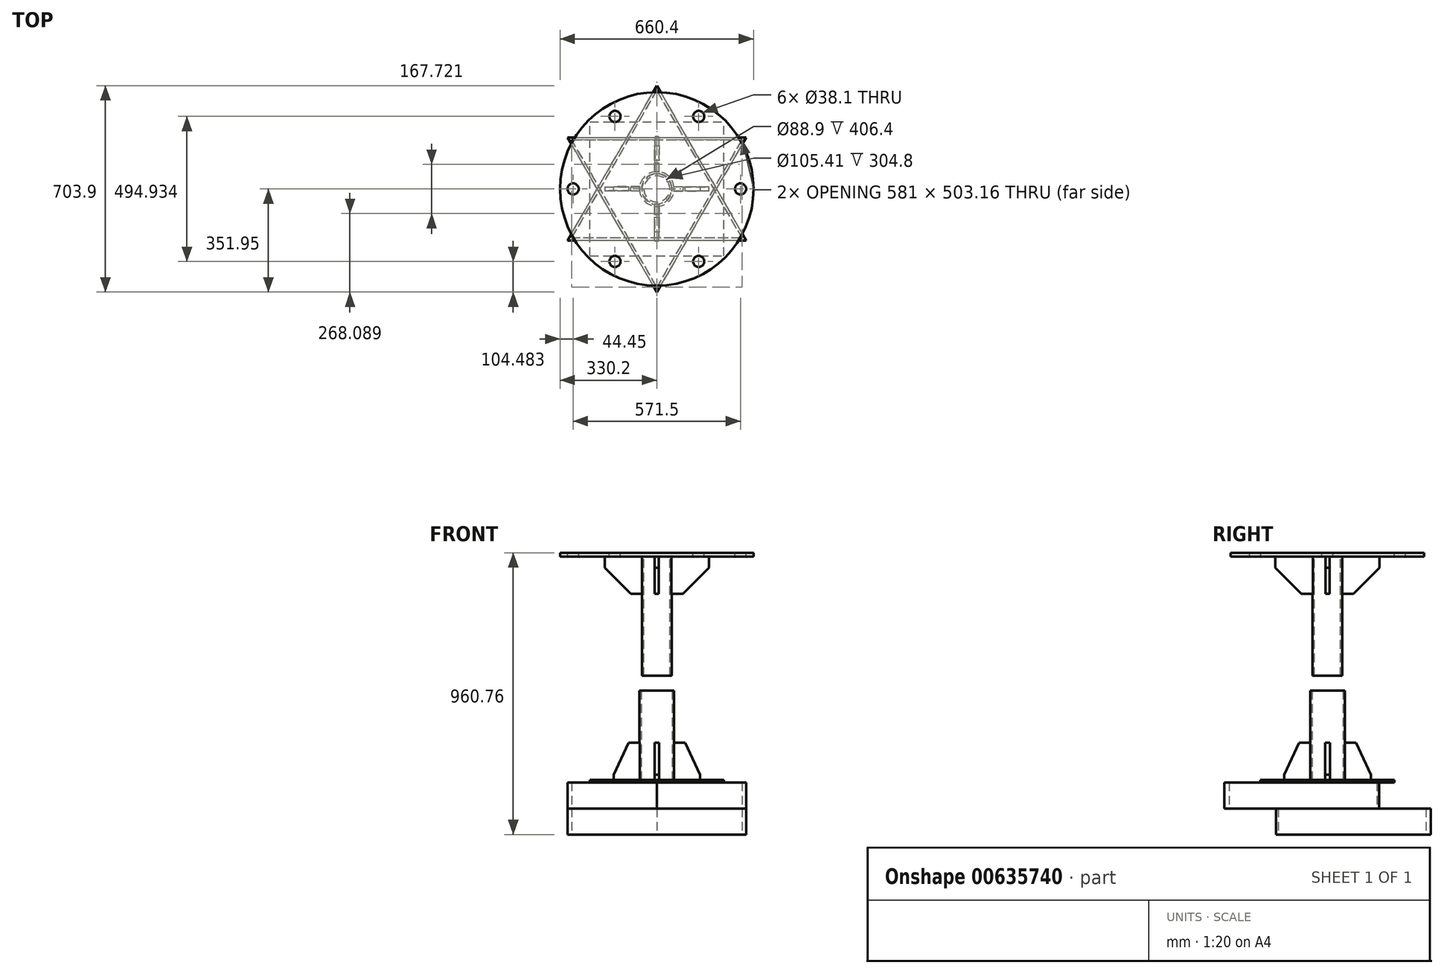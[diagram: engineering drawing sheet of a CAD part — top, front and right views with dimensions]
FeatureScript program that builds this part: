
annotation { "Feature Type Name" : "Feature", "Feature Type Description" : "" }
export const myFeature = defineFeature(function(context is Context, id is Id, definition is map)
    precondition{}
    {
        {
            var Q0;
            Q0=qCreatedBy(makeId("Top.planeOp"),FACE);
            var sketch = newSketch(context, id + "F0", { "sketchPlane" : qUnion([Q0])});
            skPoint(sketch, "E0.middle", {"position": v(0, 0) * mm});
            skCircle(sketch, "E1.cCircle", {"center": v(0, 0) * mm, "radius": 175.98 * mm, "construction": true});
            skLineSegment(sketch, "E1.0", {"start": v(304.8, -175.98) * mm, "end": v(-304.8, -175.98) * mm});
            skLineSegment(sketch, "E1.1", {"start": v(-304.8, -175.98) * mm, "end": v(0, 351.95) * mm});
            skLineSegment(sketch, "E1.2", {"start": v(0, 351.95) * mm, "end": v(304.8, -175.98) * mm});
            skPoint(sketch, "E1.0.midPoint", {"position": v(0, -175.98) * mm});
            skPoint(sketch, "E2.0.midPoint", {"position": v(-152.4, -87.99) * mm});
            skLineSegment(sketch, "E3.0", {"start": v(-290.5, -167.72) * mm, "end": v(0, 335.44) * mm});
            skLineSegment(sketch, "E3.1", {"start": v(290.5, -167.72) * mm, "end": v(-290.5, -167.72) * mm});
            skLineSegment(sketch, "E3.2", {"start": v(0, 335.44) * mm, "end": v(290.5, -167.72) * mm});
            skSolve(sketch);
        }
        {
            var Q0;
            Q0=qSketchRegion(id+"F0",true);
            var Q1;
            Q1=qConstructionFilter(qBodyType(qCreatedBy(id+"F0",EDGE),BodyType.WIRE),ConstructionObject.NO);
            extrude(context, id + "F1", {"entities" : qUnion([Q0]), "surfaceEntities" : qUnion([Q1]), "depth" : 88.9 * mm, "offsetDistance" : 25.4 * mm});
        }
        {
            var Q0;
            Q0=qCreatedBy(makeId("Top.planeOp"),FACE);
            cPlane(context, id + "F2", {"entities" : qUnion([Q0]), "cplaneType" : CPlaneType.OFFSET, "offset" : 88.9 * mm, "width" : 152.4 * mm, "height" : 152.4 * mm});
        }
        {
            var Q0;
            Q0=qCreatedBy(id+"F2.planeOp",FACE);
            var sketch = newSketch(context, id + "F3", { "sketchPlane" : qUnion([Q0])});
            skCircle(sketch, "E4.cCircle", {"center": v(0, 0) * mm, "radius": 175.98 * mm, "construction": true});
            skLineSegment(sketch, "E4.0", {"start": v(0, -351.95) * mm, "end": v(-304.8, 175.98) * mm});
            skLineSegment(sketch, "E4.1", {"start": v(-304.8, 175.98) * mm, "end": v(304.8, 175.98) * mm});
            skLineSegment(sketch, "E4.2", {"start": v(304.8, 175.98) * mm, "end": v(0, -351.95) * mm});
            skPoint(sketch, "E4.0.midPoint", {"position": v(-152.4, -87.99) * mm});
            skLineSegment(sketch, "E5.0", {"start": v(-290.5, 167.72) * mm, "end": v(290.5, 167.72) * mm});
            skLineSegment(sketch, "E5.1", {"start": v(0, -335.44) * mm, "end": v(-290.5, 167.72) * mm});
            skLineSegment(sketch, "E5.2", {"start": v(290.5, 167.72) * mm, "end": v(0, -335.44) * mm});
            skSolve(sketch);
        }
        {
            var Q0;
            Q0=qSketchRegion(id+"F3",true);
            extrude(context, id + "F4", {"entities" : qUnion([Q0]), "depth" : 88.9 * mm, "offsetDistance" : 25.4 * mm});
        }
        {
            var Q0;
            Q0=makeQuery(id+"F4.opExtrude","CAP_FACE",FACE,{"disambiguationData":[OSD([sQuery(id+"F3.wireOp",EDGE,"E4.0"),sQuery(id+"F3.wireOp",EDGE,"E4.1"),sQuery(id+"F3.wireOp",EDGE,"E4.2"),sQuery(id+"F3.wireOp",EDGE,"E5.0"),sQuery(id+"F3.wireOp",EDGE,"E5.1"),sQuery(id+"F3.wireOp",EDGE,"E5.2")])],"isStart":false});
            var sketch = newSketch(context, id + "F5", { "sketchPlane" : qUnion([Q0])});
            skLineSegment(sketch, "E6.bottom", {"start": v(108.95, 167.72) * mm, "end": v(70.85, 167.72) * mm});
            skLineSegment(sketch, "E6.top", {"start": v(108.95, -162.48) * mm, "end": v(70.85, -162.48) * mm});
            skLineSegment(sketch, "E6.left", {"start": v(108.95, 167.72) * mm, "end": v(108.95, -162.48) * mm});
            skLineSegment(sketch, "E6.right", {"start": v(70.85, 167.72) * mm, "end": v(70.85, -162.48) * mm});
            skLineSegment(sketch, "E7.bottom", {"start": v(-99.89, 167.72) * mm, "end": v(-61.79, 167.72) * mm});
            skLineSegment(sketch, "E7.top", {"start": v(-99.89, -162.48) * mm, "end": v(-61.79, -162.48) * mm});
            skLineSegment(sketch, "E7.left", {"start": v(-99.89, 167.72) * mm, "end": v(-99.89, -162.48) * mm});
            skLineSegment(sketch, "E7.right", {"start": v(-61.79, 167.72) * mm, "end": v(-61.79, -162.48) * mm});
            skSolve(sketch);
        }
        {
            var Q0;
            Q0=qSketchRegion(id+"F5",true);
            extrude(context, id + "F6", {"entities" : qUnion([Q0]), "depth" : 17.78 * mm, "offsetDistance" : 25.4 * mm});
        }
        {
            var Q0;
            Q0=makeQuery(id+"F4.opExtrude","CAP_FACE",FACE,{"disambiguationData":[OSD([sQuery(id+"F3.wireOp",EDGE,"E4.0"),sQuery(id+"F3.wireOp",EDGE,"E4.1"),sQuery(id+"F3.wireOp",EDGE,"E4.2"),sQuery(id+"F3.wireOp",EDGE,"E5.0"),sQuery(id+"F3.wireOp",EDGE,"E5.1"),sQuery(id+"F3.wireOp",EDGE,"E5.2")])],"isStart":false});
            var sketch = newSketch(context, id + "F7", { "sketchPlane" : qUnion([Q0])});
            skLineSegment(sketch, "E8.bottom", {"start": v(-228.6, -228.6) * mm, "end": v(228.6, -228.6) * mm});
            skLineSegment(sketch, "E8.top", {"start": v(-228.6, 228.6) * mm, "end": v(228.6, 228.6) * mm});
            skLineSegment(sketch, "E8.left", {"start": v(-228.6, -228.6) * mm, "end": v(-228.6, 228.6) * mm});
            skLineSegment(sketch, "E8.right", {"start": v(228.6, -228.6) * mm, "end": v(228.6, 228.6) * mm});
            skPoint(sketch, "E8.middle", {"position": v(0, 0) * mm});
            skSolve(sketch);
        }
        {
            var Q0;
            Q0=qSketchRegion(id+"F7",true);
            extrude(context, id + "F8", {"entities" : qUnion([Q0]), "depth" : 8.25 * mm, "offsetDistance" : 25.4 * mm});
        }
        {
            var Q0;
            Q0=makeQuery(id+"F8.opExtrude","CAP_FACE",FACE,{"disambiguationData":[OSD([sQuery(id+"F7.wireOp",EDGE,"E8.bottom"),sQuery(id+"F7.wireOp",EDGE,"E8.top"),sQuery(id+"F7.wireOp",EDGE,"E8.left"),sQuery(id+"F7.wireOp",EDGE,"E8.right")])],"isStart":false});
            var sketch = newSketch(context, id + "F9", { "sketchPlane" : qUnion([Q0])});
            skCircle(sketch, "E9", {"center": v(0, 0) * mm, "radius": 52.7 * mm});
            skCircle(sketch, "E10.0", {"center": v(0, 0) * mm, "radius": 59.06 * mm});
            skLineSegment(sketch, "E11.bottom", {"start": v(58.54, -7.78) * mm, "end": v(147.44, -7.78) * mm});
            skLineSegment(sketch, "E11.top", {"start": v(58.54, 7.78) * mm, "end": v(147.44, 7.78) * mm});
            skLineSegment(sketch, "E11.right", {"start": v(147.44, -7.78) * mm, "end": v(147.44, 7.78) * mm});
            skPoint(sketch, "E11.middle", {"position": v(103, 0) * mm});
            skLineSegment(sketch, "E12.1.0", {"start": v(-7.78, 58.54) * mm, "end": v(-7.78, 147.44) * mm});
            skLineSegment(sketch, "E12.1.1", {"start": v(7.78, 58.54) * mm, "end": v(7.78, 147.44) * mm});
            skLineSegment(sketch, "E12.1.2", {"start": v(7.78, 147.44) * mm, "end": v(-7.78, 147.44) * mm});
            skLineSegment(sketch, "E12.2.0", {"start": v(-58.54, -7.78) * mm, "end": v(-147.44, -7.78) * mm});
            skLineSegment(sketch, "E12.2.1", {"start": v(-58.54, 7.78) * mm, "end": v(-147.44, 7.78) * mm});
            skLineSegment(sketch, "E12.2.2", {"start": v(-147.44, 7.78) * mm, "end": v(-147.44, -7.78) * mm});
            skLineSegment(sketch, "E13.1.3.0", {"start": v(7.78, -58.54) * mm, "end": v(7.78, -147.44) * mm});
            skLineSegment(sketch, "E13.3.3.0", {"start": v(-7.78, -58.54) * mm, "end": v(-7.78, -147.44) * mm});
            skLineSegment(sketch, "E13.6.3.0", {"start": v(-7.78, -147.44) * mm, "end": v(7.78, -147.44) * mm});
            skSolve(sketch);
        }
        {
            var Q0;
            Q0=makeQuery(id+"F9.imprint","IMPRINT",FACE,{"disambiguationData":[TD([[makeQuery(id+"F9.imprint","IMPRINT",EDGE,{"derivedFrom":sQuery(id+"F9.wireOp",EDGE,"E9")}),-1.0]])]});
            extrude(context, id + "F10", {"entities" : qUnion([Q0]), "depth" : 304.8 * mm, "offsetDistance" : 25.4 * mm});
        }
        {
            var Q0;
            {var subQ0=sQuery(id+"F9.wireOp",EDGE,"E12.2.0");Q0=makeQuery(id+"F9.imprint","IMPRINT",FACE,{"disambiguationData":[TD([[makeQuery(id+"F9.imprint","IMPRINT",EDGE,{"derivedFrom":subQ0}),-1.0]])]});}
            var Q1;
            {var subQ0=sQuery(id+"F9.wireOp",EDGE,"E13.1.3.0");Q1=makeQuery(id+"F9.imprint","IMPRINT",FACE,{"disambiguationData":[TD([[makeQuery(id+"F9.imprint","IMPRINT",EDGE,{"derivedFrom":subQ0}),-1.0]])]});}
            var Q2;
            {var subQ0=sQuery(id+"F9.wireOp",EDGE,"E12.1.0");Q2=makeQuery(id+"F9.imprint","IMPRINT",FACE,{"disambiguationData":[TD([[makeQuery(id+"F9.imprint","IMPRINT",EDGE,{"derivedFrom":subQ0}),-1.0]])]});}
            var Q3;
            {var subQ1=sQuery(id+"F9.wireOp",EDGE,"E11.bottom");Q3=makeQuery(id+"F9.imprint","IMPRINT",FACE,{"disambiguationData":[TD([[makeQuery(id+"F9.imprint","IMPRINT",EDGE,{"derivedFrom":subQ1}),1.0]])]});}
            extrude(context, id + "F11", {"entities" : qUnion([Q0, Q1, Q2, Q3]), "depth" : 127 * mm, "offsetDistance" : 25.4 * mm});
        }
        {
            var Q0;
            Q0=makeQuery(id+"F11.opExtrude","CAP_EDGE",EDGE,{"disambiguationData":[OSD([sQuery(id+"F9.wireOp",EDGE,"E11.right")])],"isStart":false});
            var Q1;
            Q1=makeQuery(id+"F11.opExtrude","CAP_EDGE",EDGE,{"disambiguationData":[OSD([sQuery(id+"F9.wireOp",EDGE,"E13.6.3.0")])],"isStart":false});
            var Q2;
            Q2=makeQuery(id+"F11.opExtrude","CAP_EDGE",EDGE,{"disambiguationData":[OSD([sQuery(id+"F9.wireOp",EDGE,"E12.2.2")])],"isStart":false});
            var Q3;
            Q3=makeQuery(id+"F11.opExtrude","CAP_EDGE",EDGE,{"disambiguationData":[OSD([sQuery(id+"F9.wireOp",EDGE,"E12.1.2")])],"isStart":false});
            chamfer(context, id + "F12", {"entities" : qUnion([Q0, Q1, Q2, Q3]), "chamferType" : ChamferType.OFFSET_ANGLE, "width" : 50.8 * mm, "oppositeDirection" : false, "angle" : 65 * degree, "tangentPropagation" : true});
        }
        {
            var Q0;
            Q0=makeQuery(id+"F10.opExtrude","CAP_FACE",FACE,{"disambiguationData":[OSD([sQuery(id+"F9.wireOp",EDGE,"E9"),sQuery(id+"F9.wireOp",EDGE,"E10.0"),sQuery(id+"F9.wireOp",EDGE,"E11.left")])],"isStart":false});
            cPlane(context, id + "F13", {"entities" : qUnion([Q0]), "cplaneType" : CPlaneType.OFFSET, "offset" : 457.2 * mm, "width" : 152.4 * mm, "height" : 152.4 * mm});
        }
        {
            var Q0;
            Q0=qCreatedBy(id+"F13.planeOp",FACE);
            var sketch = newSketch(context, id + "F14", { "sketchPlane" : qUnion([Q0])});
            skCircle(sketch, "E14", {"center": v(0, 0) * mm, "radius": 44.45 * mm});
            skCircle(sketch, "E15.0", {"center": v(0, 0) * mm, "radius": 50.8 * mm});
            skCircle(sketch, "E16", {"center": v(0, 0) * mm, "radius": 330.2 * mm});
            skLineSegment(sketch, "E17.bottom", {"start": v(-177.8, -6.63) * mm, "end": v(-50.37, -6.63) * mm});
            skLineSegment(sketch, "E17.top", {"start": v(-177.8, 6.83) * mm, "end": v(-50.34, 6.83) * mm});
            skLineSegment(sketch, "E17.left", {"start": v(-177.8, -6.63) * mm, "end": v(-177.8, 6.83) * mm});
            skPoint(sketch, "E17.middle", {"position": v(-80.74, 0) * mm});
            skLineSegment(sketch, "E18.1.0", {"start": v(6.83, 177.8) * mm, "end": v(6.83, 50.34) * mm});
            skLineSegment(sketch, "E18.1.1", {"start": v(-6.63, 177.8) * mm, "end": v(-6.63, 50.37) * mm});
            skLineSegment(sketch, "E18.1.2", {"start": v(-6.63, 177.8) * mm, "end": v(6.83, 177.8) * mm});
            skLineSegment(sketch, "E18.2.0", {"start": v(177.8, -6.83) * mm, "end": v(50.34, -6.83) * mm});
            skLineSegment(sketch, "E18.2.1", {"start": v(177.8, 6.63) * mm, "end": v(50.37, 6.63) * mm});
            skLineSegment(sketch, "E18.2.2", {"start": v(177.8, 6.63) * mm, "end": v(177.8, -6.83) * mm});
            skLineSegment(sketch, "E18.3.0", {"start": v(-6.83, -177.8) * mm, "end": v(-6.83, -50.34) * mm});
            skLineSegment(sketch, "E18.3.1", {"start": v(6.63, -177.8) * mm, "end": v(6.63, -50.37) * mm});
            skLineSegment(sketch, "E18.3.2", {"start": v(6.63, -177.8) * mm, "end": v(-6.83, -177.8) * mm});
            skLineSegment(sketch, "E18.anchor1", {"start": v(0, 0) * mm, "end": v(-177.8, 6.83) * mm, "construction": true});
            skLineSegment(sketch, "E18.anchor2", {"start": v(0, 0) * mm, "end": v(-6.83, -177.8) * mm, "construction": true});
            skSolve(sketch);
        }
        {
            var Q0;
            {var subQ0=sQuery(id+"F14.wireOp",EDGE,"E18.1.0");Q0=makeQuery(id+"F14.imprint","IMPRINT",FACE,{"disambiguationData":[TD([[makeQuery(id+"F14.imprint","IMPRINT",EDGE,{"derivedFrom":subQ0}),-1.0]])]});}
            var Q1;
            {var subQ0=sQuery(id+"F14.wireOp",EDGE,"E17.bottom");Q1=makeQuery(id+"F14.imprint","IMPRINT",FACE,{"disambiguationData":[TD([[makeQuery(id+"F14.imprint","IMPRINT",EDGE,{"derivedFrom":subQ0}),1.0]])]});}
            var Q2;
            {var subQ0=sQuery(id+"F14.wireOp",EDGE,"E18.3.0");Q2=makeQuery(id+"F14.imprint","IMPRINT",FACE,{"disambiguationData":[TD([[makeQuery(id+"F14.imprint","IMPRINT",EDGE,{"derivedFrom":subQ0}),-1.0]])]});}
            var Q3;
            {var subQ0=sQuery(id+"F14.wireOp",EDGE,"E18.2.0");Q3=makeQuery(id+"F14.imprint","IMPRINT",FACE,{"disambiguationData":[TD([[makeQuery(id+"F14.imprint","IMPRINT",EDGE,{"derivedFrom":subQ0}),-1.0]])]});}
            extrude(context, id + "F15", {"entities" : qUnion([Q0, Q1, Q2, Q3]), "oppositeDirection" : true, "depth" : 127 * mm, "offsetDistance" : 25.4 * mm});
        }
        {
            var Q0;
            Q0=makeQuery(id+"F14.imprint","IMPRINT",FACE,{"disambiguationData":[TD([[makeQuery(id+"F14.imprint","IMPRINT",EDGE,{"derivedFrom":sQuery(id+"F14.wireOp",EDGE,"E14")}),-1.0]])]});
            extrude(context, id + "F16", {"entities" : qUnion([Q0]), "oppositeDirection" : true, "depth" : 406.4 * mm, "offsetDistance" : 25.4 * mm});
        }
        {
            var Q0;
            Q0=makeQuery(id+"F14.imprint","IMPRINT",FACE,{"disambiguationData":[TD([[makeQuery(id+"F14.imprint","IMPRINT",EDGE,{"derivedFrom":sQuery(id+"F14.wireOp",EDGE,"E16")}),1.0]])]});
            var Q1;
            Q1=makeQuery(id+"F14.imprint","IMPRINT",FACE,{"disambiguationData":[TD([[makeQuery(id+"F14.imprint","IMPRINT",EDGE,{"derivedFrom":sQuery(id+"F14.wireOp",EDGE,"E14")}),-1.0]])]});
            var Q2;
            {var subQ0=sQuery(id+"F14.wireOp",EDGE,"E18.3.0");Q2=makeQuery(id+"F14.imprint","IMPRINT",FACE,{"disambiguationData":[TD([[makeQuery(id+"F14.imprint","IMPRINT",EDGE,{"derivedFrom":subQ0}),-1.0]])]});}
            var Q3;
            {var subQ0=sQuery(id+"F14.wireOp",EDGE,"E18.2.0");Q3=makeQuery(id+"F14.imprint","IMPRINT",FACE,{"disambiguationData":[TD([[makeQuery(id+"F14.imprint","IMPRINT",EDGE,{"derivedFrom":subQ0}),-1.0]])]});}
            var Q4;
            {var subQ0=sQuery(id+"F14.wireOp",EDGE,"E17.bottom");Q4=makeQuery(id+"F14.imprint","IMPRINT",FACE,{"disambiguationData":[TD([[makeQuery(id+"F14.imprint","IMPRINT",EDGE,{"derivedFrom":subQ0}),1.0]])]});}
            var Q5;
            {var subQ0=sQuery(id+"F14.wireOp",EDGE,"E18.1.0");Q5=makeQuery(id+"F14.imprint","IMPRINT",FACE,{"disambiguationData":[TD([[makeQuery(id+"F14.imprint","IMPRINT",EDGE,{"derivedFrom":subQ0}),-1.0]])]});}
            var Q6;
            Q6=makeQuery(id+"F14.imprint","IMPRINT",FACE,{"disambiguationData":[TD([[makeQuery(id+"F14.imprint","IMPRINT",EDGE,{"derivedFrom":sQuery(id+"F14.wireOp",EDGE,"E14")}),1.0]])]});
            extrude(context, id + "F17", {"entities" : qUnion([Q0, Q1, Q2, Q3, Q4, Q5, Q6]), "depth" : 12.7 * mm, "offsetDistance" : 25.4 * mm});
        }
        {
            var Q0;
            Q0=makeQuery(id+"F15.opExtrude","CAP_EDGE",EDGE,{"disambiguationData":[OSD([sQuery(id+"F14.wireOp",EDGE,"E18.1.2")])],"isStart":false});
            var Q1;
            Q1=makeQuery(id+"F15.opExtrude","CAP_EDGE",EDGE,{"disambiguationData":[OSD([sQuery(id+"F14.wireOp",EDGE,"E18.2.2")])],"isStart":false});
            var Q2;
            Q2=makeQuery(id+"F15.opExtrude","CAP_EDGE",EDGE,{"disambiguationData":[OSD([sQuery(id+"F14.wireOp",EDGE,"E17.left")])],"isStart":false});
            var Q3;
            Q3=makeQuery(id+"F15.opExtrude","CAP_EDGE",EDGE,{"disambiguationData":[OSD([sQuery(id+"F14.wireOp",EDGE,"E18.3.2")])],"isStart":false});
            chamfer(context, id + "F18", {"entities" : qUnion([Q0, Q1, Q2, Q3]), "width" : 88.9 * mm, "tangentPropagation" : true});
        }
        {
            var Q0;
            Q0=makeQuery(id+"F6.opExtrude","SWEPT_BODY",BODY,{"disambiguationData":[OSD([sQuery(id+"F5.wireOp",EDGE,"E6.bottom"),sQuery(id+"F5.wireOp",EDGE,"E6.top"),sQuery(id+"F5.wireOp",EDGE,"E6.left"),sQuery(id+"F5.wireOp",EDGE,"E6.right")])]});
            deleteBodies(context, id + "F19", {"entities" : qUnion([Q0])});
        }
        {
            var Q0;
            Q0=makeQuery(id+"F6.opExtrude","SWEPT_BODY",BODY,{"disambiguationData":[OSD([sQuery(id+"F5.wireOp",EDGE,"E7.bottom"),sQuery(id+"F5.wireOp",EDGE,"E7.top"),sQuery(id+"F5.wireOp",EDGE,"E7.left"),sQuery(id+"F5.wireOp",EDGE,"E7.right")])]});
            deleteBodies(context, id + "F20", {"entities" : qUnion([Q0])});
        }
        {
            var Q0;
            Q0=makeQuery(id+"F17.opExtrude","CAP_FACE",FACE,{"disambiguationData":[OSD([sQuery(id+"F14.wireOp",EDGE,"E16")])],"isStart":false});
            var sketch = newSketch(context, id + "F21", { "sketchPlane" : qUnion([Q0])});
            skCircle(sketch, "E19", {"center": v(-285.75, 0) * mm, "radius": 19.05 * mm});
            skCircle(sketch, "E20.1.0", {"center": v(-142.88, -247.47) * mm, "radius": 19.05 * mm});
            skCircle(sketch, "E20.2.0", {"center": v(142.87, -247.47) * mm, "radius": 19.05 * mm});
            skCircle(sketch, "E20.3.0", {"center": v(285.75, 0) * mm, "radius": 19.05 * mm});
            skCircle(sketch, "E20.4.0", {"center": v(142.88, 247.47) * mm, "radius": 19.05 * mm});
            skCircle(sketch, "E20.5.0", {"center": v(-142.88, 247.47) * mm, "radius": 19.05 * mm});
            skPoint(sketch, "E20.center", {"position": v(0, 0) * mm});
            skSolve(sketch);
        }
        {
            var Q0;
            Q0=makeQuery(id+"F21.imprint","IMPRINT",FACE,{"disambiguationData":[TD([[makeQuery(id+"F21.imprint","IMPRINT",EDGE,{"derivedFrom":sQuery(id+"F21.wireOp",EDGE,"E19")}),1.0]])]});
            var Q1;
            Q1=makeQuery(id+"F21.imprint","IMPRINT",FACE,{"disambiguationData":[TD([[makeQuery(id+"F21.imprint","IMPRINT",EDGE,{"derivedFrom":sQuery(id+"F21.wireOp",EDGE,"E20.5.0")}),1.0]])]});
            var Q2;
            Q2=makeQuery(id+"F21.imprint","IMPRINT",FACE,{"disambiguationData":[TD([[makeQuery(id+"F21.imprint","IMPRINT",EDGE,{"derivedFrom":sQuery(id+"F21.wireOp",EDGE,"E20.4.0")}),1.0]])]});
            var Q3;
            Q3=makeQuery(id+"F21.imprint","IMPRINT",FACE,{"disambiguationData":[TD([[makeQuery(id+"F21.imprint","IMPRINT",EDGE,{"derivedFrom":sQuery(id+"F21.wireOp",EDGE,"E20.3.0")}),1.0]])]});
            var Q4;
            Q4=makeQuery(id+"F21.imprint","IMPRINT",FACE,{"disambiguationData":[TD([[makeQuery(id+"F21.imprint","IMPRINT",EDGE,{"derivedFrom":sQuery(id+"F21.wireOp",EDGE,"E20.2.0")}),1.0]])]});
            var Q5;
            Q5=makeQuery(id+"F21.imprint","IMPRINT",FACE,{"disambiguationData":[TD([[makeQuery(id+"F21.imprint","IMPRINT",EDGE,{"derivedFrom":sQuery(id+"F21.wireOp",EDGE,"E20.1.0")}),1.0]])]});
            extrude(context, id + "F22", {"entities" : qUnion([Q0, Q1, Q2, Q3, Q4, Q5]), "operationType" : NewBodyOperationType.REMOVE, "endBound" : BoundingType.THROUGH_ALL, "oppositeDirection" : true, "depth" : 25.4 * mm, "offsetDistance" : 25.4 * mm});
        }
    });
